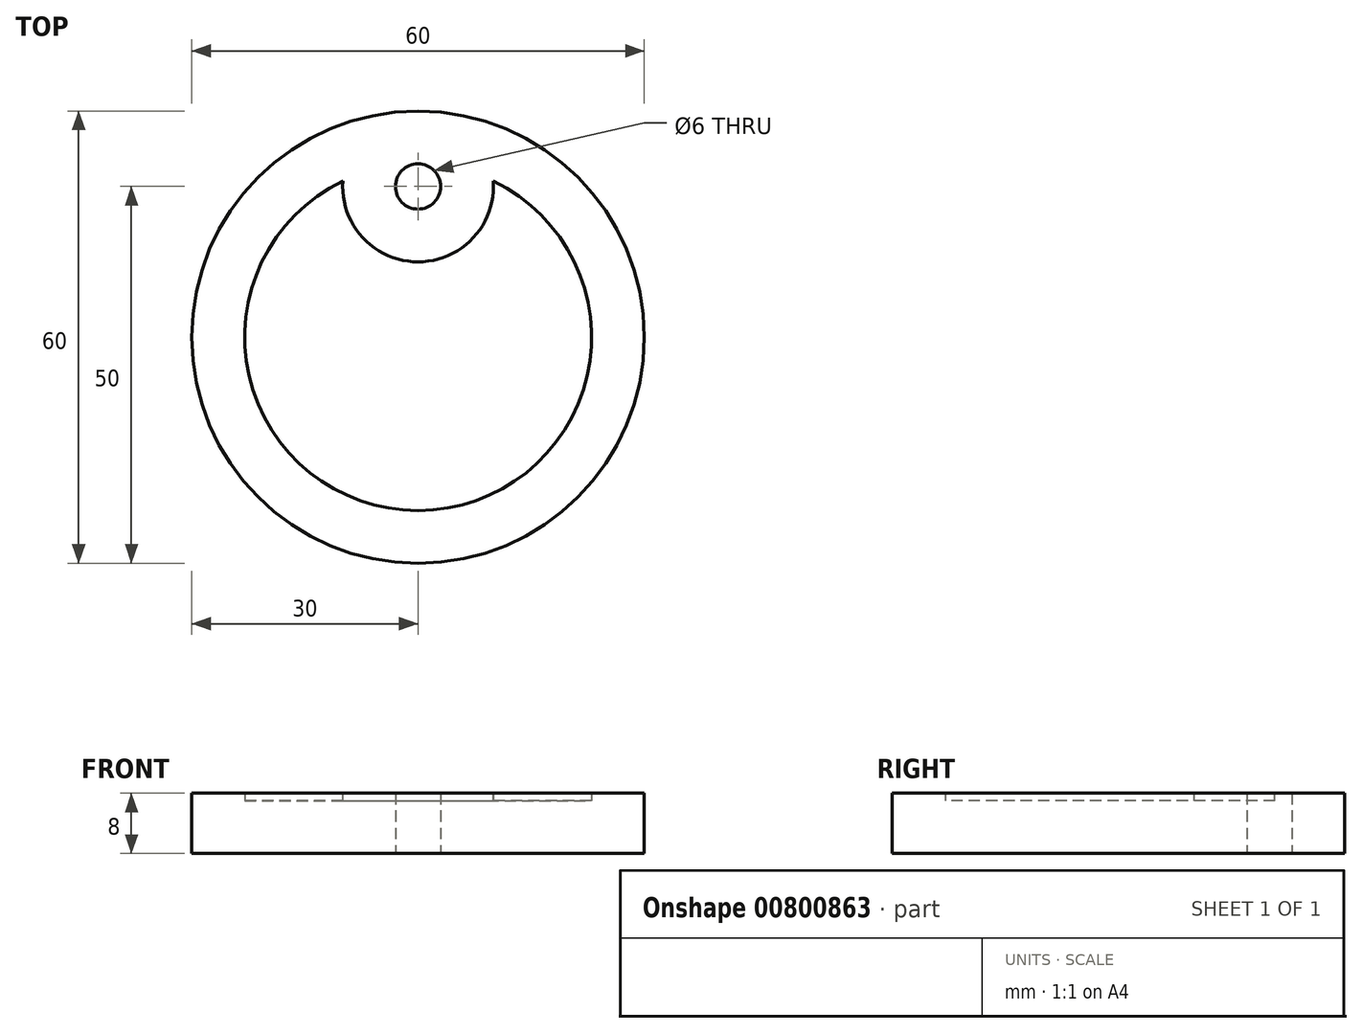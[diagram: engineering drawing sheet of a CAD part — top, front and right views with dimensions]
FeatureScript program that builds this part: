
annotation { "Feature Type Name" : "Feature", "Feature Type Description" : "" }
export const myFeature = defineFeature(function(context is Context, id is Id, definition is map)
    precondition{}
    {
        {
            var Q0;
            Q0=qCreatedBy(makeId("Top.planeOp"),FACE);
            var sketch = newSketch(context, id + "F0", { "sketchPlane" : qUnion([Q0])});
            skCircle(sketch, "E0", {"center": v(0, 0) * mm, "radius": 30 * mm});
            skCircle(sketch, "E1", {"center": v(0, 0) * mm, "radius": 20 * mm, "construction": true});
            skLineSegment(sketch, "E2", {"start": v(0, 0) * mm, "end": v(0, 30) * mm, "construction": true});
            skCircle(sketch, "E3", {"center": v(0, 20) * mm, "radius": 3 * mm});
            skSolve(sketch);
        }
        {
            var Q0;
            Q0=makeQuery(id+"F0.imprint","IMPRINT",FACE,{"disambiguationData":[TD([[makeQuery(id+"F0.imprint","IMPRINT",EDGE,{"derivedFrom":sQuery(id+"F0.wireOp",EDGE,"E0")}),1.0]])]});
            extrude(context, id + "F1", {"entities" : qUnion([Q0]), "depth" : 8 * mm, "offsetDistance" : 25 * mm});
        }
        {
            var Q0;
            Q0=makeQuery(id+"F1.opExtrude","CAP_FACE",FACE,{"disambiguationData":[OSD([sQuery(id+"F0.wireOp",EDGE,"E0"),sQuery(id+"F0.wireOp",EDGE,"E3")])],"isStart":false});
            shell(context, id + "F2", {"entities" : qUnion([Q0]), "thickness" : 7 * mm});
        }
    });
